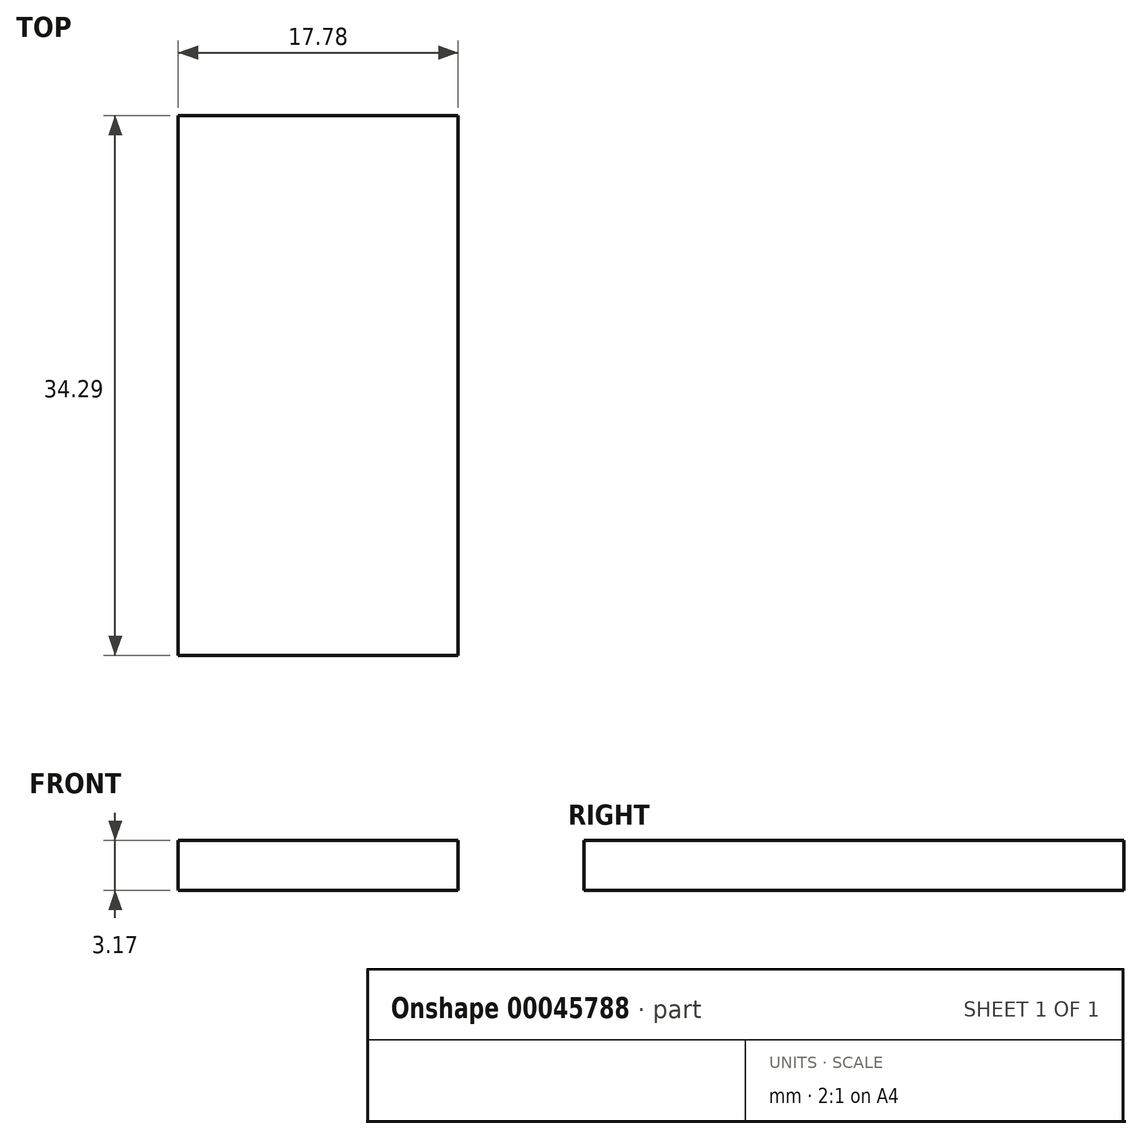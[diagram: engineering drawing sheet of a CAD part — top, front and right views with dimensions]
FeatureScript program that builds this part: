
annotation { "Feature Type Name" : "Feature", "Feature Type Description" : "" }
export const myFeature = defineFeature(function(context is Context, id is Id, definition is map)
    precondition{}
    {
        {
            var Q0;
            Q0=qCreatedBy(makeId("Top.planeOp"),FACE);
            var sketch = newSketch(context, id + "F0", { "sketchPlane" : qUnion([Q0])});
            skLineSegment(sketch, "E0.rect.bottom", {"start": v(-8.89, 16.8) * mm, "end": v(8.9, 16.8) * mm});
            skLineSegment(sketch, "E0.rect.top", {"start": v(-8.9, -17.48) * mm, "end": v(8.89, -17.48) * mm});
            skLineSegment(sketch, "E0.rect.left", {"start": v(-8.89, 16.8) * mm, "end": v(-8.9, -17.48) * mm});
            skLineSegment(sketch, "E0.rect.right", {"start": v(8.9, 16.8) * mm, "end": v(8.89, -17.48) * mm});
            skPoint(sketch, "E0.rect.middle", {"position": v(0, -0.34) * mm});
            skSolve(sketch);
        }
        {
            var Q0;
            Q0=makeQuery(id+"F0.imprint","IMPRINT",FACE,{"disambiguationData":[TD([[makeQuery(id+"F0.imprint","IMPRINT",EDGE,{"derivedFrom":sQuery(id+"F0.wireOp",EDGE,"E0.rect.bottom")}),-1.0]])]});
            extrude(context, id + "F1", {"entities" : qUnion([Q0]), "depth" : 3.17 * mm});
        }
    });
